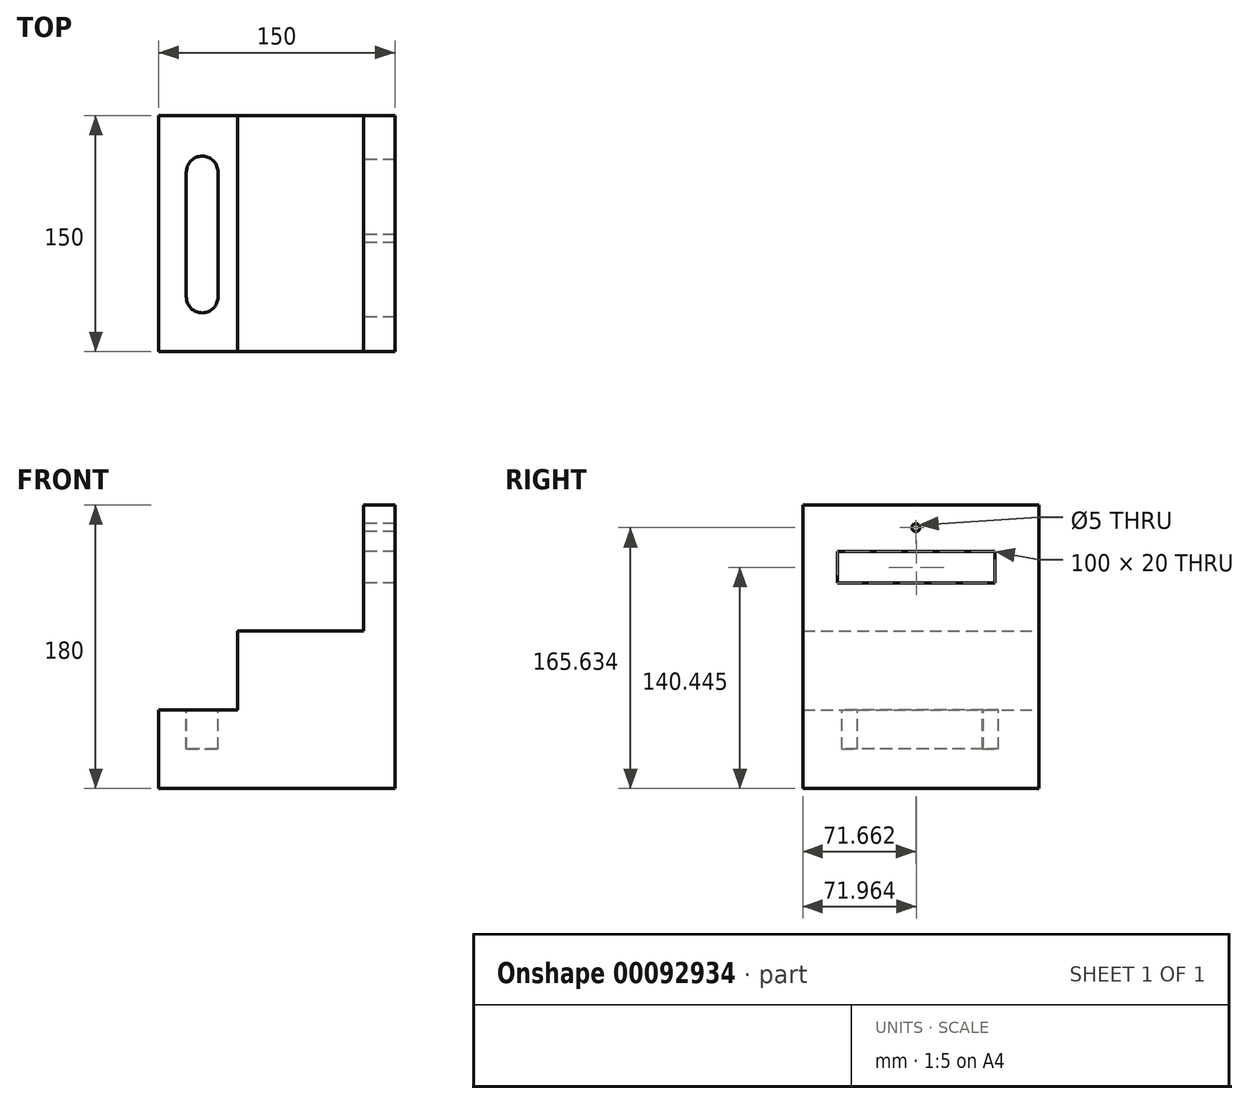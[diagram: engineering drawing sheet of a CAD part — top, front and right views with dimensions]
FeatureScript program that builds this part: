
annotation { "Feature Type Name" : "Feature", "Feature Type Description" : "" }
export const myFeature = defineFeature(function(context is Context, id is Id, definition is map)
    precondition{}
    {
        {
            var Q0;
            Q0=qCreatedBy(makeId("Front.planeOp"),FACE);
            var sketch = newSketch(context, id + "F0", { "sketchPlane" : qUnion([Q0])});
            skLineSegment(sketch, "E0.bottom", {"start": v(75, 90) * mm, "end": v(55, 90) * mm});
            skLineSegment(sketch, "E0.top", {"start": v(75, -90) * mm, "end": v(-75, -90) * mm});
            skLineSegment(sketch, "E0.left", {"start": v(75, 90) * mm, "end": v(75, -90) * mm});
            skLineSegment(sketch, "E0.right", {"start": v(-75, -40) * mm, "end": v(-75, -90) * mm});
            skPoint(sketch, "E0.middle", {"position": v(0, 0) * mm});
            skLineSegment(sketch, "E1", {"start": v(55, 90) * mm, "end": v(55, 10) * mm});
            skLineSegment(sketch, "E2", {"start": v(55, 10) * mm, "end": v(-25, 10) * mm});
            skLineSegment(sketch, "E3", {"start": v(-25, 10) * mm, "end": v(-25, -40) * mm});
            skLineSegment(sketch, "E4", {"start": v(-25, -40) * mm, "end": v(-75, -40) * mm});
            skPoint(sketch, "E5.orphan", {"position": v(-75, 90) * mm});
            skSolve(sketch);
        }
        {
            var Q0;
            Q0 = qSketchRegion(id + "F0", true);
            var Q1;
            Q1=makeQuery(id+"F0.imprint","IMPRINT",FACE,{"disambiguationData":[TD([[makeQuery(id+"F0.imprint","IMPRINT",EDGE,{"derivedFrom":sQuery(id+"F0.wireOp",EDGE,"E0.top")}),-1.0]])]});
            extrude(context, id + "F1", {"entities" : qUnion([Q0, Q1]), "depth" : 150 * mm});
        }
        {
            var Q0;
            Q0=makeQuery(id+"F1.opExtrude","SWEPT_FACE",FACE,{"disambiguationData":[OSD([sQuery(id+"F0.wireOp",EDGE,"E1")])]});
            var sketch = newSketch(context, id + "F2", { "sketchPlane" : qUnion([Q0])});
            skLineSegment(sketch, "E6.bottom", {"start": v(28.04, 60.44) * mm, "end": v(128.04, 60.44) * mm});
            skLineSegment(sketch, "E6.top", {"start": v(28.04, 40.44) * mm, "end": v(128.04, 40.44) * mm});
            skLineSegment(sketch, "E6.left", {"start": v(28.04, 60.44) * mm, "end": v(28.04, 40.44) * mm});
            skLineSegment(sketch, "E6.right", {"start": v(128.04, 60.44) * mm, "end": v(128.04, 40.44) * mm});
            skPoint(sketch, "E6.middle", {"position": v(78.04, 50.44) * mm});
            skSolve(sketch);
        }
        {
            var Q0;
            Q0=makeQuery(id+"F2.imprint","IMPRINT",FACE,{"disambiguationData":[TD([[makeQuery(id+"F2.imprint","IMPRINT",EDGE,{"derivedFrom":sQuery(id+"F2.wireOp",EDGE,"E6.bottom")}),-1.0]])]});
            extrude(context, id + "F3", {"entities" : qUnion([Q0]), "operationType" : NewBodyOperationType.REMOVE, "endBound" : BoundingType.THROUGH_ALL, "oppositeDirection" : true, "depth" : 20 * mm});
        }
        {
            var Q0;
            Q0=makeQuery(id+"F1.opExtrude","SWEPT_FACE",FACE,{"disambiguationData":[OSD([sQuery(id+"F0.wireOp",EDGE,"E4")])]});
            var sketch = newSketch(context, id + "F4", { "sketchPlane" : qUnion([Q0])});
            skLineSegment(sketch, "E7.bottom", {"start": v(-37.51, -35.56) * mm, "end": v(-57.51, -35.56) * mm});
            skLineSegment(sketch, "E7.top", {"start": v(-37.51, -115.56) * mm, "end": v(-57.51, -115.56) * mm});
            skLineSegment(sketch, "E7.left", {"start": v(-37.51, -35.56) * mm, "end": v(-37.51, -115.56) * mm});
            skLineSegment(sketch, "E7.right", {"start": v(-57.51, -35.56) * mm, "end": v(-57.51, -115.56) * mm});
            skPoint(sketch, "E7.middle", {"position": v(-47.51, -75.56) * mm});
            skSolve(sketch);
        }
        {
            var Q0;
            Q0=makeQuery(id+"F4.imprint","IMPRINT",FACE,{"disambiguationData":[TD([[makeQuery(id+"F4.imprint","IMPRINT",EDGE,{"derivedFrom":sQuery(id+"F4.wireOp",EDGE,"E7.bottom")}),1.0]])]});
            var sketch = newSketch(context, id + "F5", { "sketchPlane" : qUnion([Q0])});
            skArc(sketch, "E8", {"start": v(-37.4, -35.97) * mm, "mid": v(-47.4, -25.86) * mm, "end": v(-57.4, -35.97) * mm});
            skArc(sketch, "E9", {"start": v(-57.4, -115.42) * mm, "mid": v(-47.4, -125.42) * mm, "end": v(-37.4, -115.42) * mm});
            skLineSegment(sketch, "E10", {"start": v(-37.4, -35.97) * mm, "end": v(-37.4, -115.42) * mm});
            skLineSegment(sketch, "E11", {"start": v(-57.4, -35.97) * mm, "end": v(-57.4, -115.42) * mm});
            skSolve(sketch);
        }
        {
            var Q0;
            Q0=makeQuery(id+"F4.imprint","IMPRINT",FACE,{"disambiguationData":[TD([[makeQuery(id+"F4.imprint","IMPRINT",EDGE,{"derivedFrom":sQuery(id+"F4.wireOp",EDGE,"E7.bottom")}),1.0]])]});
            extrude(context, id + "F6", {"entities" : qUnion([Q0]), "operationType" : NewBodyOperationType.REMOVE, "oppositeDirection" : true, "depth" : 25 * mm});
        }
        {
            var Q0;
            {var subQ1=sQuery(id+"F5.wireOp",EDGE,"E10");Q0=makeQuery(id+"F5.imprint","IMPRINT",FACE,{"disambiguationData":[TD([[makeQuery(id+"F5.imprint","IMPRINT",EDGE,{"derivedFrom":subQ1}),-1.0]])]});}
            extrude(context, id + "F7", {"entities" : qUnion([Q0]), "operationType" : NewBodyOperationType.REMOVE, "oppositeDirection" : true, "depth" : 25 * mm});
        }
        {
            var Q0;
            Q0=makeQuery(id+"F1.opExtrude","SWEPT_FACE",FACE,{"disambiguationData":[OSD([sQuery(id+"F0.wireOp",EDGE,"E1")])]});
            var sketch = newSketch(context, id + "F8", { "sketchPlane" : qUnion([Q0])});
            skCircle(sketch, "E12", {"center": v(78.34, 75.63) * mm, "radius": 2.5 * mm});
            skSolve(sketch);
        }
        {
            var Q0;
            Q0=makeQuery(id+"F8.imprint","IMPRINT",FACE,{"disambiguationData":[TD([[makeQuery(id+"F8.imprint","IMPRINT",EDGE,{"derivedFrom":sQuery(id+"F8.wireOp",EDGE,"E12")}),1.0]])]});
            extrude(context, id + "F9", {"entities" : qUnion([Q0]), "operationType" : NewBodyOperationType.REMOVE, "endBound" : BoundingType.THROUGH_ALL, "oppositeDirection" : true, "depth" : 25.4 * mm});
        }
    });
